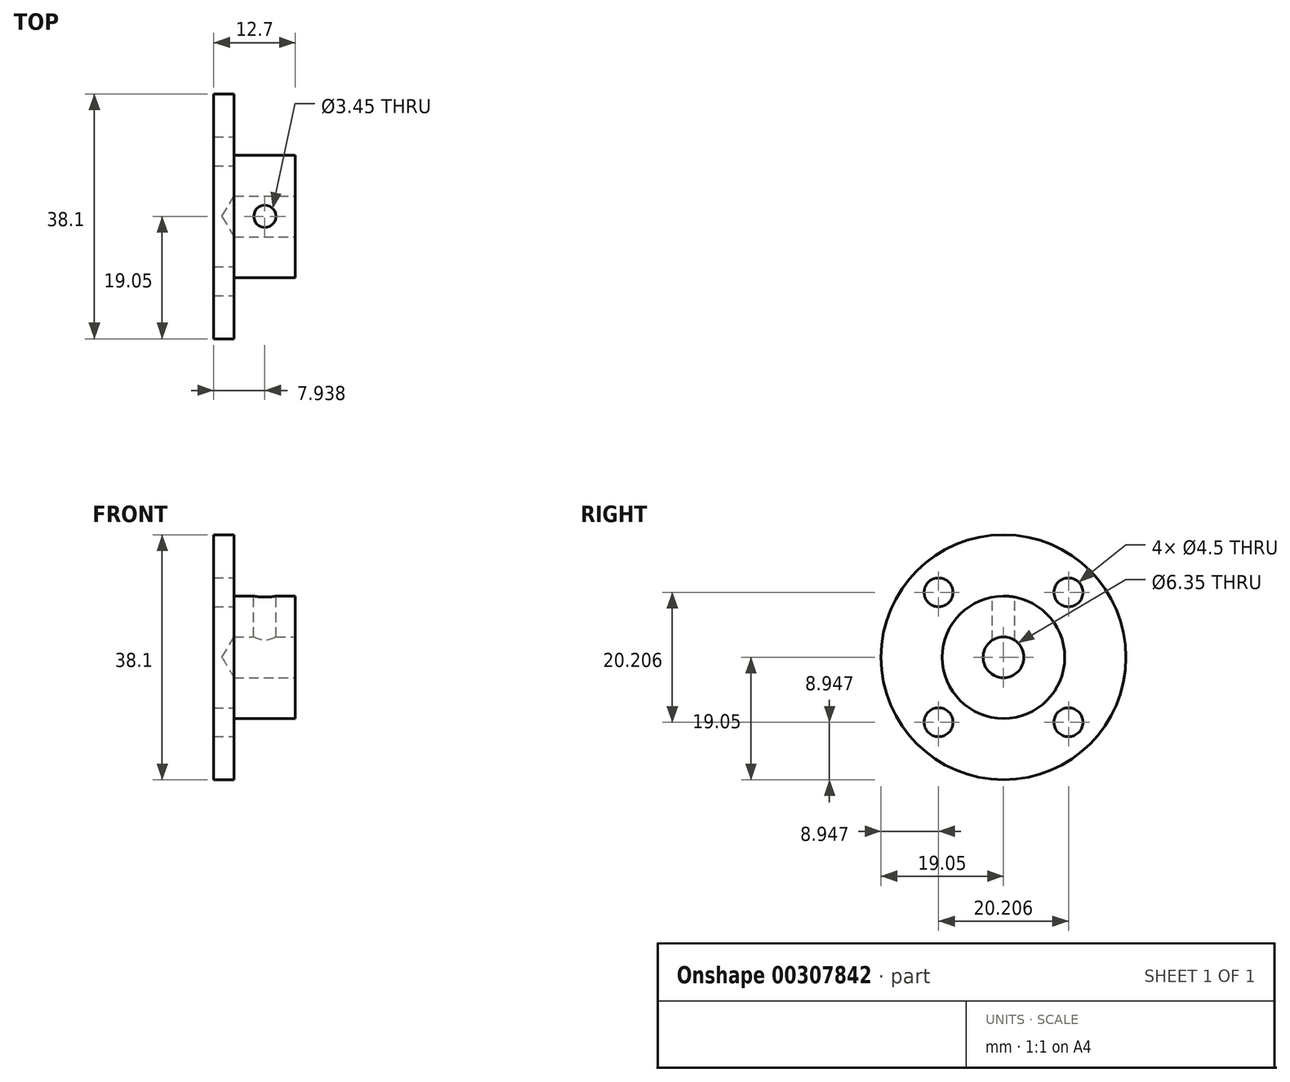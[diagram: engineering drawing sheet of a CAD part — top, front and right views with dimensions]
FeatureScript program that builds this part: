
annotation { "Feature Type Name" : "Feature", "Feature Type Description" : "" }
export const myFeature = defineFeature(function(context is Context, id is Id, definition is map)
    precondition{}
    {
        {
            var Q0;
            Q0=qCreatedBy(makeId("Right.planeOp"),FACE);
            var sketch = newSketch(context, id + "F0", { "sketchPlane" : qUnion([Q0])});
            skCircle(sketch, "E0", {"center": v(0, 0) * mm, "radius": 19.05 * mm});
            skSolve(sketch);
        }
        {
            var Q0;
            Q0=makeQuery(id+"F0.imprint","IMPRINT",FACE,{"disambiguationData":[TD([[makeQuery(id+"F0.imprint","IMPRINT",EDGE,{"derivedFrom":sQuery(id+"F0.wireOp",EDGE,"E0")}),1.0]])]});
            extrude(context, id + "F1", {"entities" : qUnion([Q0]), "depth" : 3.17 * mm});
        }
        {
            var Q0;
            Q0=makeQuery(id+"F1.opExtrude","CAP_FACE",FACE,{"disambiguationData":[OSD([sQuery(id+"F0.wireOp",EDGE,"E0")])],"isStart":false});
            var sketch = newSketch(context, id + "F2", { "sketchPlane" : qUnion([Q0])});
            skCircle(sketch, "E1", {"center": v(0, 0) * mm, "radius": 9.53 * mm});
            skSolve(sketch);
        }
        {
            var Q0;
            Q0=makeQuery(id+"F2.imprint","IMPRINT",FACE,{"disambiguationData":[TD([[makeQuery(id+"F2.imprint","IMPRINT",EDGE,{"derivedFrom":sQuery(id+"F2.wireOp",EDGE,"E1")}),1.0]])]});
            extrude(context, id + "F3", {"entities" : qUnion([Q0]), "operationType" : NewBodyOperationType.ADD, "depth" : 9.52 * mm});
        }
        {
            var Q0;
            Q0=makeQuery(id+"F3.opExtrude","CAP_FACE",FACE,{"disambiguationData":[OSD([sQuery(id+"F2.wireOp",EDGE,"E1")])],"isStart":false});
            var sketch = newSketch(context, id + "F4", { "sketchPlane" : qUnion([Q0])});
            skPoint(sketch, "E2", {"position": v(0, 0) * mm});
            skSolve(sketch);
        }
        {
            var Q0;
            Q0=sQuery(id+"F4.wireOp",VERTEX,"E2");
            var Q1;
            Q1=makeQuery(id+"F1.opExtrude","SWEPT_BODY",BODY,{"disambiguationData":[OSD([sQuery(id+"F0.wireOp",EDGE,"E0")])]});
            hole(context, id + "F5", {"style" : HoleStyle.SIMPLE, "endStyle" : HoleEndStyle.BLIND, "holeDiameter" : 6.35 * mm, "holeDepth" : 9.52 * mm, "tappedDepth" : 12.7 * mm, "tapClearance" : 3, "locations" : qUnion([Q0]), "scope" : qUnion([Q1])});
        }
        {
            var Q0;
            Q0=qCreatedBy(makeId("Top.planeOp"),FACE);
            cPlane(context, id + "F6", {"entities" : qUnion([Q0]), "cplaneType" : CPlaneType.OFFSET, "offset" : 9.52 * mm, "width" : 152.4 * mm, "height" : 152.4 * mm});
        }
        {
            var Q0;
            Q0=qCreatedBy(id+"F6.planeOp",FACE);
            var sketch = newSketch(context, id + "F7", { "sketchPlane" : qUnion([Q0])});
            skPoint(sketch, "E3", {"position": v(7.94, 0) * mm});
            skSolve(sketch);
        }
        {
            var Q0;
            Q0=sQuery(id+"F7.wireOp",VERTEX,"E3");
            var Q1;
            Q1=makeQuery(id+"F1.opExtrude","SWEPT_BODY",BODY,{"disambiguationData":[OSD([sQuery(id+"F0.wireOp",EDGE,"E0")])]});
            hole(context, id + "F8", {"style" : HoleStyle.SIMPLE, "endStyle" : HoleEndStyle.BLIND, "standardTappedOrClearance" : lookupTablePath({ "standard" : "ANSI", "engagement" : "75%", "pitch" : "32 tpi", "size" : "#8", "type" : "Tapped" }), "standardBlindInLast" : lookupTablePath({ "standard" : "ANSI", "engagement" : "75%", "pitch" : "32 tpi", "size" : "#8", "type" : "Tapped" }), "holeDiameter" : 3.45 * mm, "showTappedDepth" : true, "holeDepth" : 9.52 * mm, "tappedDepth" : 7.14 * mm, "tapClearance" : 3, "locations" : qUnion([Q0]), "scope" : qUnion([Q1]), "majorDiameter" : 4.17 * mm});
        }
        {
            var Q0;
            Q0=makeQuery(id+"F1.opExtrude","CAP_FACE",FACE,{"disambiguationData":[OSD([sQuery(id+"F0.wireOp",EDGE,"E0")])],"isStart":false});
            var sketch = newSketch(context, id + "F9", { "sketchPlane" : qUnion([Q0])});
            skCircle(sketch, "E4", {"center": v(0, 0) * mm, "radius": 14.29 * mm});
            skLineSegment(sketch, "E5", {"start": v(0, 0) * mm, "end": v(13.47, 13.47) * mm, "construction": true});
            skPoint(sketch, "E6", {"position": v(10.1, 10.1) * mm});
            skPoint(sketch, "E7.1.0", {"position": v(-10.1, 10.1) * mm});
            skPoint(sketch, "E7.2.0", {"position": v(-10.1, -10.1) * mm});
            skPoint(sketch, "E7.3.0", {"position": v(10.1, -10.1) * mm});
            skSolve(sketch);
        }
        {
            var Q0;
            Q0=sQuery(id+"F9.wireOp",VERTEX,"E7.1.0");
            var Q1;
            Q1=sQuery(id+"F9.wireOp",VERTEX,"E6");
            var Q2;
            Q2=sQuery(id+"F9.wireOp",VERTEX,"E7.3.0");
            var Q3;
            Q3=sQuery(id+"F9.wireOp",VERTEX,"E7.2.0");
            var Q4;
            Q4=makeQuery(id+"F1.opExtrude","SWEPT_BODY",BODY,{"disambiguationData":[OSD([sQuery(id+"F0.wireOp",EDGE,"E0")])]});
            hole(context, id + "F10", {"style" : HoleStyle.SIMPLE, "endStyle" : HoleEndStyle.THROUGH, "standardTappedOrClearance" : lookupTablePath({ "standard" : "ANSI", "fit" : "Normal (ASME)", "size" : "#8", "type" : "Clearance" }), "standardBlindInLast" : lookupTablePath({ "fit" : "Free", "standard" : "ANSI", "size" : "#8", "type" : "Clearance" }), "holeDiameter" : 4.5 * mm, "tappedDepth" : 18.26 * mm, "tapClearance" : 1, "locations" : qUnion([Q0, Q1, Q2, Q3]), "scope" : qUnion([Q4])});
        }
    });
